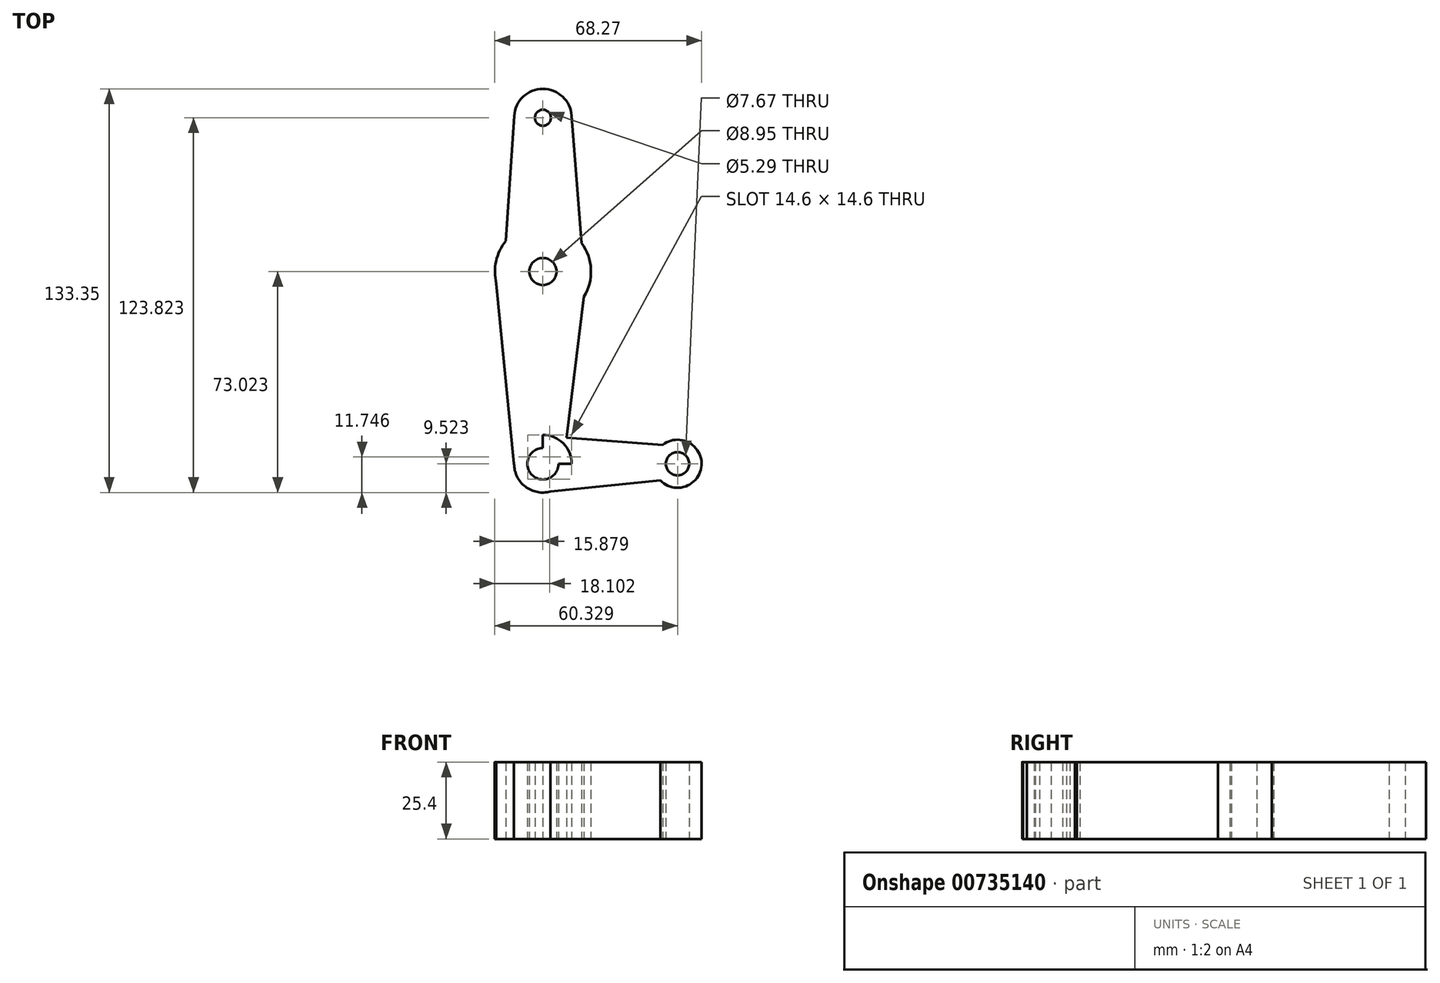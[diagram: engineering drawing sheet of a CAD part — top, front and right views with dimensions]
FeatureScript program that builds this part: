
annotation { "Feature Type Name" : "Feature", "Feature Type Description" : "" }
export const myFeature = defineFeature(function(context is Context, id is Id, definition is map)
    precondition{}
    {
        {
            var Q0;
            Q0=qCreatedBy(makeId("Top.planeOp"),FACE);
            var sketch = newSketch(context, id + "F0", { "sketchPlane" : qUnion([Q0])});
            skLineSegment(sketch, "E0", {"start": v(-72.41, 58.13) * mm, "end": v(-72.41, -56.17) * mm});
            skLineSegment(sketch, "E1", {"start": v(-72.41, -56.17) * mm, "end": v(-27.96, -56.17) * mm});
            skCircle(sketch, "E2", {"center": v(-72.41, 58.13) * mm, "radius": 9.53 * mm});
            skCircle(sketch, "E3", {"center": v(-72.41, -56.17) * mm, "radius": 9.52 * mm});
            skCircle(sketch, "E4", {"center": v(-27.96, -56.17) * mm, "radius": 7.94 * mm});
            skCircle(sketch, "E5", {"center": v(-72.41, 7.33) * mm, "radius": 15.88 * mm});
            skLineSegment(sketch, "E6", {"start": v(-87.79, 3.4) * mm, "end": v(-81.94, -56.15) * mm});
            skLineSegment(sketch, "E7", {"start": v(-69.9, -65.36) * mm, "end": v(-33.68, -61.68) * mm});
            skLineSegment(sketch, "E8", {"start": v(-62.9, 58.79) * mm, "end": v(-59.64, 16.77) * mm});
            skLineSegment(sketch, "E9", {"start": v(-58.88, -0.97) * mm, "end": v(-64.98, -50.2) * mm});
            skCircle(sketch, "E10", {"center": v(-72.41, 58.13) * mm, "radius": 2.65 * mm});
            skCircle(sketch, "E11", {"center": v(-72.41, 7.33) * mm, "radius": 4.47 * mm});
            skCircle(sketch, "E12", {"center": v(-27.96, -56.17) * mm, "radius": 3.83 * mm});
            skCircle(sketch, "E13", {"center": v(-72.41, -56.17) * mm, "radius": 5.18 * mm});
            skLineSegment(sketch, "E14", {"start": v(-81.92, 58.76) * mm, "end": v(-84.65, 17.44) * mm});
            skLineSegment(sketch, "E15", {"start": v(-32.87, -49.93) * mm, "end": v(-69.13, -47.22) * mm});
            skSolve(sketch);
        }
        {
            var Q0;
            Q0 = qSketchRegion(id + "F0", true);
            extrude(context, id + "F1", {"entities" : qUnion([Q0]), "depth" : 25.4 * mm, "offsetDistance" : 25.4 * mm});
        }
    });
